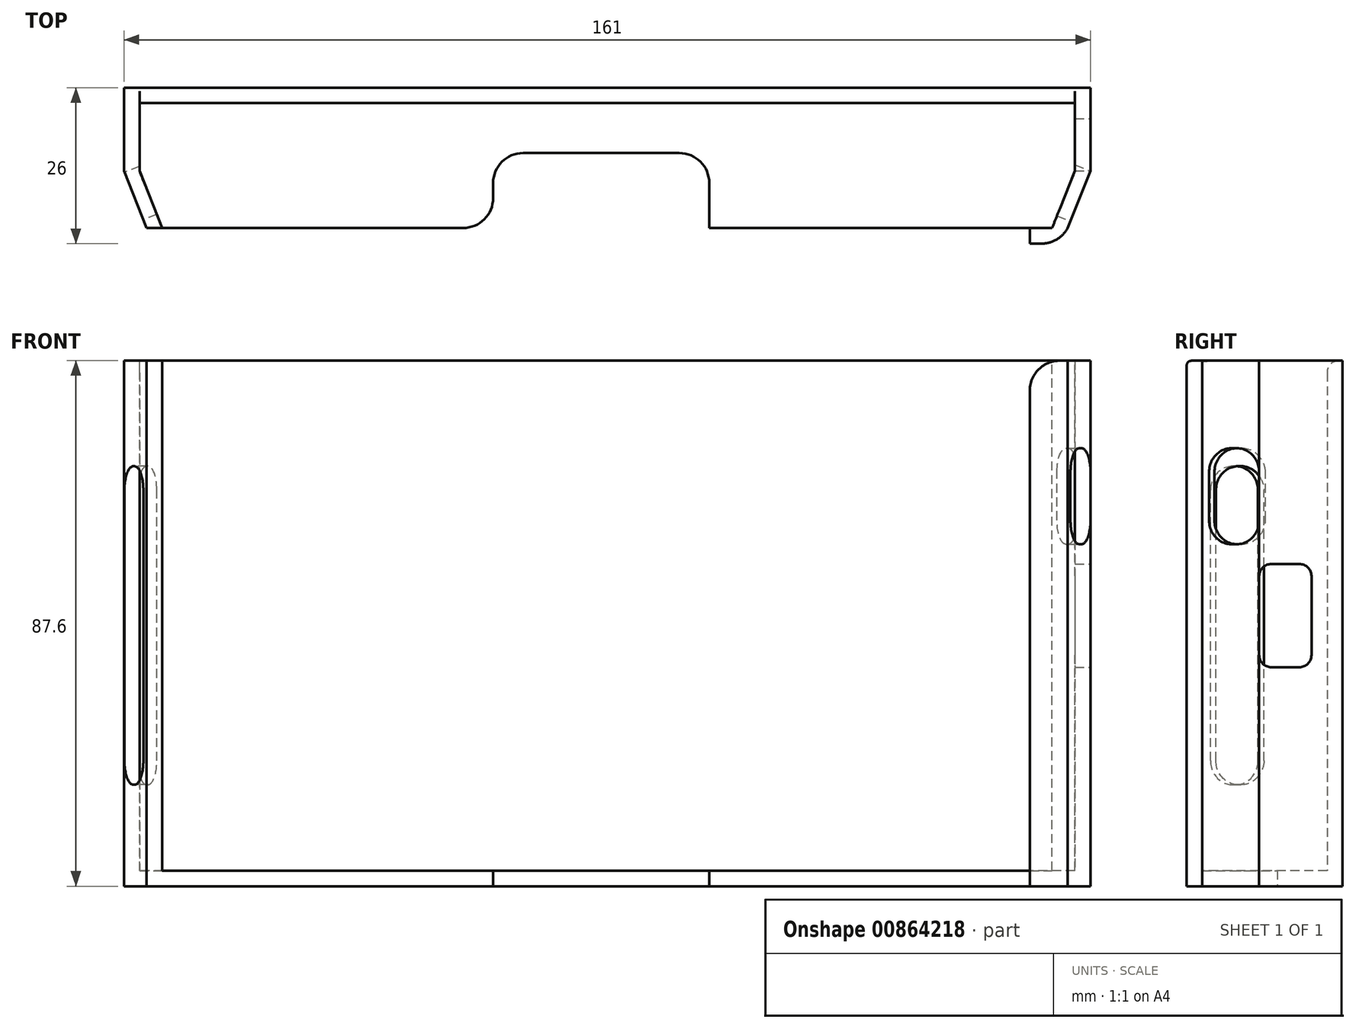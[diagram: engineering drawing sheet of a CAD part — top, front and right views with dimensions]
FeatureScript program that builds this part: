
annotation { "Feature Type Name" : "Feature", "Feature Type Description" : "" }
export const myFeature = defineFeature(function(context is Context, id is Id, definition is map)
    precondition{}
    {
        {
            var Q0;
            Q0=qCreatedBy(makeId("Front.planeOp"),FACE);
            var sketch = newSketch(context, id + "F0", { "sketchPlane" : qUnion([Q0])});
            skLineSegment(sketch, "E0.bottom", {"start": v(77.9, 42.5) * mm, "end": v(-77.9, 42.5) * mm});
            skLineSegment(sketch, "E0.top", {"start": v(77.9, -42.5) * mm, "end": v(-77.9, -42.5) * mm});
            skLineSegment(sketch, "E0.left", {"start": v(77.9, 42.5) * mm, "end": v(77.9, -42.5) * mm});
            skLineSegment(sketch, "E0.right", {"start": v(-77.9, 42.5) * mm, "end": v(-77.9, -42.5) * mm});
            skPoint(sketch, "E0.middle", {"position": v(0, 0) * mm});
            skSolve(sketch);
        }
        {
            var Q0;
            Q0=makeQuery(id+"F0.imprint","IMPRINT",FACE,{"disambiguationData":[TD([[makeQuery(id+"F0.imprint","IMPRINT",EDGE,{"derivedFrom":sQuery(id+"F0.wireOp",EDGE,"E0.bottom")}),1.0]])]});
            extrude(context, id + "F1", {"entities" : qUnion([Q0]), "depth" : 2.6 * mm, "offsetDistance" : 25 * mm});
        }
        {
            var Q0;
            Q0=makeQuery(id+"F1.opExtrude","SWEPT_FACE",FACE,{"disambiguationData":[OSD([sQuery(id+"F0.wireOp",EDGE,"E0.bottom")])]});
            var sketch = newSketch(context, id + "F2", { "sketchPlane" : qUnion([Q0])});
            skLineSegment(sketch, "E1", {"start": v(-77.9, -2.6) * mm, "end": v(-77.9, -13.9) * mm});
            skLineSegment(sketch, "E2", {"start": v(-77.9, -13.9) * mm, "end": v(-80.5, -13.9) * mm});
            skLineSegment(sketch, "E3", {"start": v(-80.5, -13.9) * mm, "end": v(-80.5, 0) * mm});
            skLineSegment(sketch, "E4", {"start": v(-80.5, 0) * mm, "end": v(-77.9, 0) * mm});
            skLineSegment(sketch, "E5", {"start": v(-77.9, -13.9) * mm, "end": v(-77.9, -23.4) * mm, "construction": true});
            skLineSegment(sketch, "E6", {"start": v(-77.9, -23.4) * mm, "end": v(-74.1, -23.4) * mm, "construction": true});
            skLineSegment(sketch, "E7", {"start": v(-77.9, -13.9) * mm, "end": v(-74.1, -23.4) * mm});
            skLineSegment(sketch, "E8", {"start": v(-74.1, -23.4) * mm, "end": v(-76.7, -23.4) * mm});
            skLineSegment(sketch, "E9", {"start": v(-76.7, -23.4) * mm, "end": v(-80.5, -13.9) * mm});
            skLineSegment(sketch, "E10.MirrorCS", {"start": v(77.9, -2.6) * mm, "end": v(77.9, -13.9) * mm});
            skLineSegment(sketch, "E11.MirrorCS", {"start": v(80.5, -13.9) * mm, "end": v(80.5, 0) * mm});
            skLineSegment(sketch, "E12.MirrorCS", {"start": v(76.7, -23.4) * mm, "end": v(80.5, -13.9) * mm});
            skLineSegment(sketch, "E13.MirrorCS", {"start": v(77.9, -13.9) * mm, "end": v(74.1, -23.4) * mm});
            skLineSegment(sketch, "E14.MirrorCS", {"start": v(80.5, 0) * mm, "end": v(77.9, 0) * mm});
            skLineSegment(sketch, "E15", {"start": v(74.1, -23.4) * mm, "end": v(76.7, -23.4) * mm});
            skSolve(sketch);
        }
        {
            var Q0;
            Q0=makeQuery(id+"F2.imprint","IMPRINT",FACE,{"disambiguationData":[TD([[makeQuery(id+"F2.imprint","IMPRINT",EDGE,{"derivedFrom":sQuery(id+"F2.wireOp",EDGE,"E1")}),-1.0]])]});
            var Q1;
            Q1=makeQuery(id+"F2.imprint","IMPRINT",FACE,{"disambiguationData":[TD([[makeQuery(id+"F2.imprint","IMPRINT",EDGE,{"derivedFrom":sQuery(id+"F2.wireOp",EDGE,"E2")}),1.0]])]});
            var Q2;
            Q2=makeQuery(id+"F2.imprint","IMPRINT",FACE,{"disambiguationData":[TD([[makeQuery(id+"F2.imprint","IMPRINT",EDGE,{"derivedFrom":sQuery(id+"F2.wireOp",EDGE,"E10.MirrorCS")}),1.0]])]});
            extrude(context, id + "F3", {"entities" : qUnion([Q0, Q1, Q2]), "operationType" : NewBodyOperationType.ADD, "oppositeDirection" : true, "depth" : 85 * mm, "offsetDistance" : 25 * mm});
        }
        {
            var Q0;
            {var subQ0=sQuery(id+"F0.wireOp",EDGE,"E0.bottom");Q0=makeQuery(id+"F3.boolean.opBoolean","MERGE",FACE,{"derivedFrom":[makeQuery(id+"F1.opExtrude","SWEPT_FACE",FACE,{"disambiguationData":[OSD([sQuery(id+"F0.wireOp",EDGE,"E0.top")])]}),makeQuery(id+"F3.opExtrude","CAP_FACE",FACE,{"disambiguationData":[OSD([subQ0,sQuery(id+"F0.wireOp",EDGE,"E0.right"),sQuery(id+"F2.wireOp",EDGE,"E1"),sQuery(id+"F2.wireOp",EDGE,"E3"),sQuery(id+"F2.wireOp",EDGE,"E4"),sQuery(id+"F2.wireOp",EDGE,"E7"),sQuery(id+"F2.wireOp",EDGE,"E8"),sQuery(id+"F2.wireOp",EDGE,"E9")])],"isStart":false}),makeQuery(id+"F3.opExtrude","CAP_FACE",FACE,{"disambiguationData":[OSD([subQ0,sQuery(id+"F0.wireOp",EDGE,"E0.left"),sQuery(id+"F2.wireOp",EDGE,"E10.MirrorCS"),sQuery(id+"F2.wireOp",EDGE,"E11.MirrorCS"),sQuery(id+"F2.wireOp",EDGE,"E12.MirrorCS"),sQuery(id+"F2.wireOp",EDGE,"E13.MirrorCS"),sQuery(id+"F2.wireOp",EDGE,"E14.MirrorCS"),sQuery(id+"F2.wireOp",EDGE,"E15")])],"isStart":false})]});}
            var sketch = newSketch(context, id + "F4", { "sketchPlane" : qUnion([Q0])});
            skLineSegment(sketch, "E16", {"start": v(-74.1, 23.4) * mm, "end": v(74.1, 23.4) * mm});
            skLineSegment(sketch, "E17", {"start": v(74.1, 23.4) * mm, "end": v(76.7, 23.4) * mm});
            skLineSegment(sketch, "E18", {"start": v(76.7, 23.4) * mm, "end": v(80.5, 13.9) * mm});
            skLineSegment(sketch, "E19", {"start": v(80.5, 13.9) * mm, "end": v(80.5, 0) * mm});
            skLineSegment(sketch, "E20", {"start": v(80.5, 0) * mm, "end": v(-80.5, 0) * mm});
            skLineSegment(sketch, "E21", {"start": v(-80.5, 0) * mm, "end": v(-80.5, 13.9) * mm});
            skLineSegment(sketch, "E22", {"start": v(-80.5, 13.9) * mm, "end": v(-76.7, 23.4) * mm});
            skLineSegment(sketch, "E23", {"start": v(-76.7, 23.4) * mm, "end": v(-74.1, 23.4) * mm});
            skSolve(sketch);
        }
        {
            var Q0;
            Q0=makeQuery(id+"F4.imprint","IMPRINT",FACE,{"disambiguationData":[TD([[makeQuery(id+"F4.imprint","IMPRINT",EDGE,{"derivedFrom":sQuery(id+"F4.wireOp",EDGE,"E16")}),-1.0]])]});
            var Q1;
            Q1=makeQuery(id+"F4.imprint","IMPRINT",FACE,{"disambiguationData":[TD([[makeQuery(id+"F4.imprint","IMPRINT",EDGE,{"derivedFrom":sQuery(id+"F4.wireOp",EDGE,"E17")}),-1.0]])]});
            extrude(context, id + "F5", {"entities" : qUnion([Q0, Q1]), "operationType" : NewBodyOperationType.ADD, "depth" : 2.6 * mm, "offsetDistance" : 25 * mm});
        }
        {
            var Q0;
            Q0=makeQuery(id+"F5.boolean.opBoolean","MERGE",FACE,{"derivedFrom":[makeQuery(id+"F3.opExtrude","SWEPT_FACE",FACE,{"disambiguationData":[OSD([sQuery(id+"F2.wireOp",EDGE,"E11.MirrorCS")])]}),makeQuery(id+"F5.opExtrude","SWEPT_FACE",FACE,{"disambiguationData":[OSD([sQuery(id+"F4.wireOp",EDGE,"E19")])]})]});
            var sketch = newSketch(context, id + "F6", { "sketchPlane" : qUnion([Q0])});
            skLineSegment(sketch, "E24.bottom", {"start": v(-13.9, 8.6) * mm, "end": v(-5.2, 8.6) * mm});
            skLineSegment(sketch, "E24.top", {"start": v(-13.9, -8.6) * mm, "end": v(-5.2, -8.6) * mm});
            skLineSegment(sketch, "E24.left", {"start": v(-13.9, 8.6) * mm, "end": v(-13.9, -8.6) * mm});
            skLineSegment(sketch, "E24.right", {"start": v(-5.2, 8.6) * mm, "end": v(-5.2, -8.6) * mm});
            skSolve(sketch);
        }
        {
            var Q0;
            Q0=makeQuery(id+"F6.imprint","IMPRINT",FACE,{"disambiguationData":[TD([[makeQuery(id+"F6.imprint","IMPRINT",EDGE,{"derivedFrom":sQuery(id+"F6.wireOp",EDGE,"E24.bottom")}),-1.0]])]});
            extrude(context, id + "F7", {"entities" : qUnion([Q0]), "operationType" : NewBodyOperationType.REMOVE, "oppositeDirection" : true, "depth" : 25 * mm, "offsetDistance" : 25 * mm});
        }
        {
            var Q0;
            Q0=makeQuery(id+"F5.boolean.opBoolean","MERGE",FACE,{"derivedFrom":[makeQuery(id+"F3.opExtrude","SWEPT_FACE",FACE,{"disambiguationData":[OSD([sQuery(id+"F2.wireOp",EDGE,"E12.MirrorCS")])]}),makeQuery(id+"F5.opExtrude","SWEPT_FACE",FACE,{"disambiguationData":[OSD([sQuery(id+"F4.wireOp",EDGE,"E18")])]})]});
            var sketch = newSketch(context, id + "F8", { "sketchPlane" : qUnion([Q0])});
            skLineSegment(sketch, "E25.bottom", {"start": v(17, 27.9) * mm, "end": v(8, 27.9) * mm});
            skLineSegment(sketch, "E25.top", {"start": v(17, 11.9) * mm, "end": v(8, 11.9) * mm});
            skLineSegment(sketch, "E25.left", {"start": v(17, 27.9) * mm, "end": v(17, 11.9) * mm});
            skLineSegment(sketch, "E25.right", {"start": v(8, 27.9) * mm, "end": v(8, 11.9) * mm});
            skSolve(sketch);
        }
        {
            var Q0;
            Q0=makeQuery(id+"F8.imprint","IMPRINT",FACE,{"disambiguationData":[TD([[makeQuery(id+"F8.imprint","IMPRINT",EDGE,{"derivedFrom":sQuery(id+"F8.wireOp",EDGE,"E25.bottom")}),1.0]])]});
            extrude(context, id + "F9", {"entities" : qUnion([Q0]), "operationType" : NewBodyOperationType.REMOVE, "oppositeDirection" : true, "depth" : 25 * mm, "offsetDistance" : 25 * mm});
        }
        {
            var Q0;
            Q0=makeQuery(id+"F5.boolean.opBoolean","MERGE",FACE,{"derivedFrom":[makeQuery(id+"F3.opExtrude","SWEPT_FACE",FACE,{"disambiguationData":[OSD([sQuery(id+"F2.wireOp",EDGE,"E9")])]}),makeQuery(id+"F5.opExtrude","SWEPT_FACE",FACE,{"disambiguationData":[OSD([sQuery(id+"F4.wireOp",EDGE,"E22")])]})]});
            var sketch = newSketch(context, id + "F10", { "sketchPlane" : qUnion([Q0])});
            skLineSegment(sketch, "E26.bottom", {"start": v(-8.26, -28.2) * mm, "end": v(-16.76, -28.2) * mm});
            skLineSegment(sketch, "E26.top", {"start": v(-8.26, 24.9) * mm, "end": v(-16.76, 24.9) * mm});
            skLineSegment(sketch, "E26.left", {"start": v(-8.26, -28.2) * mm, "end": v(-8.26, 24.9) * mm});
            skLineSegment(sketch, "E26.right", {"start": v(-16.76, -28.2) * mm, "end": v(-16.76, 24.9) * mm});
            skSolve(sketch);
        }
        {
            var Q0;
            Q0=makeQuery(id+"F10.imprint","IMPRINT",FACE,{"disambiguationData":[TD([[makeQuery(id+"F10.imprint","IMPRINT",EDGE,{"derivedFrom":sQuery(id+"F10.wireOp",EDGE,"E26.bottom")}),-1.0]])]});
            extrude(context, id + "F11", {"entities" : qUnion([Q0]), "operationType" : NewBodyOperationType.REMOVE, "oppositeDirection" : true, "depth" : 25 * mm, "offsetDistance" : 25 * mm});
        }
        {
            var Q0;
            Q0=makeQuery(id+"FsZxfdEWeTOnJij_3.opBoolean","MERGE",FACE,{"derivedFrom":[makeQuery(id+"FqDJVQkYOp9GbU9_1.opExtrude","SWEPT_FACE",FACE,{"disambiguationData":[OSD([sQuery(id+"FvzB3UYrsBdap8L_1.wireOp",EDGE,"Uml6c2Dv-acHc-Gifl-ZtFl-aoH73OwEvOf2.top")])]}),makeQuery(id+"FhGYIp8tMEhZQ6G_2.boolean.opBoolean","MERGE",FACE,{"derivedFrom":[makeQuery(id+"F5.opExtrude","CAP_FACE",FACE,{"disambiguationData":[OSD([sQuery(id+"F4.wireOp",EDGE,"E16"),sQuery(id+"F4.wireOp",EDGE,"E17"),sQuery(id+"F4.wireOp",EDGE,"E18"),sQuery(id+"F4.wireOp",EDGE,"E19"),sQuery(id+"F4.wireOp",EDGE,"E20"),sQuery(id+"F4.wireOp",EDGE,"E21"),sQuery(id+"F4.wireOp",EDGE,"E22"),sQuery(id+"F4.wireOp",EDGE,"E23")])],"isStart":false}),makeQuery(id+"FhGYIp8tMEhZQ6G_2.opExtrude","SWEPT_FACE",FACE,{"disambiguationData":[OSD([sQuery(id+"FduUudokjhFXSVZ_2.wireOp",EDGE,"elEno3Yk-yd7y-Hb1z-syM6-87jU7vVd34ST.top")])]})]}),makeQuery(id+"Fz9UfncQxzrdPbm_2.opExtrude","SWEPT_FACE",FACE,{"disambiguationData":[OSD([sQuery(id+"Fw4ObimbiuuVDjj_2.wireOp",EDGE,"KRR7Us3h-wgd5-YgCl-ZbNL-mRqCgfLZCEfi.top")])]})]});
            var sketch = newSketch(context, id + "F12", { "sketchPlane" : qUnion([Q0])});
            skLineSegment(sketch, "E27.bottom", {"start": v(-19, 23.4) * mm, "end": v(17, 23.4) * mm});
            skLineSegment(sketch, "E27.top", {"start": v(-19, 10.9) * mm, "end": v(17, 10.9) * mm});
            skLineSegment(sketch, "E27.left", {"start": v(-19, 23.4) * mm, "end": v(-19, 10.9) * mm});
            skLineSegment(sketch, "E27.right", {"start": v(17, 23.4) * mm, "end": v(17, 10.9) * mm});
            skSolve(sketch);
        }
        {
            var Q0;
            Q0=makeQuery(id+"F12.imprint","IMPRINT",FACE,{"disambiguationData":[TD([[makeQuery(id+"F12.imprint","IMPRINT",EDGE,{"derivedFrom":sQuery(id+"F12.wireOp",EDGE,"E27.bottom")}),-1.0]])]});
            extrude(context, id + "F13", {"entities" : qUnion([Q0]), "operationType" : NewBodyOperationType.REMOVE, "oppositeDirection" : true, "depth" : 25 * mm, "offsetDistance" : 25 * mm});
        }
        {
            var Q0;
            Q0=makeQuery(id+"F11.boolean.opBoolean","COPY",EDGE,{"derivedFrom":makeQuery(id+"F11.opExtrude","SWEPT_EDGE",EDGE,{"disambiguationData":[OSD([sQuery(id+"F10.wireOp",EDGE,"E26.bottom"),sQuery(id+"F10.wireOp",EDGE,"E26.right")])]})});
            var Q1;
            Q1=makeQuery(id+"F11.boolean.opBoolean","COPY",EDGE,{"derivedFrom":makeQuery(id+"F11.opExtrude","SWEPT_EDGE",EDGE,{"disambiguationData":[OSD([sQuery(id+"F10.wireOp",EDGE,"E26.bottom"),sQuery(id+"F10.wireOp",EDGE,"E26.left")])]})});
            var Q2;
            Q2=makeQuery(id+"F11.boolean.opBoolean","COPY",EDGE,{"derivedFrom":makeQuery(id+"F11.opExtrude","SWEPT_EDGE",EDGE,{"disambiguationData":[OSD([sQuery(id+"F10.wireOp",EDGE,"E26.top"),sQuery(id+"F10.wireOp",EDGE,"E26.left")])]})});
            var Q3;
            Q3=makeQuery(id+"F11.boolean.opBoolean","COPY",EDGE,{"derivedFrom":makeQuery(id+"F11.opExtrude","SWEPT_EDGE",EDGE,{"disambiguationData":[OSD([sQuery(id+"F10.wireOp",EDGE,"E26.top"),sQuery(id+"F10.wireOp",EDGE,"E26.right")])]})});
            fillet(context, id + "F14", {"entities" : qUnion([Q0, Q1, Q2, Q3]), "radius" : 4 * mm, "tangentPropagation" : true, "allowEdgeOverflow" : false});
        }
        {
            var Q0;
            Q0=makeQuery(id+"F9.boolean.opBoolean","COPY",EDGE,{"derivedFrom":makeQuery(id+"F9.opExtrude","SWEPT_EDGE",EDGE,{"disambiguationData":[OSD([sQuery(id+"F8.wireOp",EDGE,"E25.top"),sQuery(id+"F8.wireOp",EDGE,"E25.right")])]})});
            var Q1;
            Q1=makeQuery(id+"F9.boolean.opBoolean","COPY",EDGE,{"derivedFrom":makeQuery(id+"F9.opExtrude","SWEPT_EDGE",EDGE,{"disambiguationData":[OSD([sQuery(id+"F2.wireOp",EDGE,"E11.MirrorCS"),sQuery(id+"F2.wireOp",EDGE,"E12.MirrorCS"),sQuery(id+"F4.wireOp",EDGE,"E18"),sQuery(id+"F4.wireOp",EDGE,"E19"),sQuery(id+"F8.wireOp",EDGE,"E25.top"),sQuery(id+"F8.wireOp",EDGE,"E25.left")])]})});
            var Q2;
            Q2=makeQuery(id+"F9.boolean.opBoolean","COPY",EDGE,{"derivedFrom":makeQuery(id+"F9.opExtrude","SWEPT_EDGE",EDGE,{"disambiguationData":[OSD([sQuery(id+"F8.wireOp",EDGE,"E25.bottom"),sQuery(id+"F8.wireOp",EDGE,"E25.right")])]})});
            var Q3;
            Q3=makeQuery(id+"F9.boolean.opBoolean","COPY",EDGE,{"derivedFrom":makeQuery(id+"F9.opExtrude","SWEPT_EDGE",EDGE,{"disambiguationData":[OSD([sQuery(id+"F2.wireOp",EDGE,"E11.MirrorCS"),sQuery(id+"F2.wireOp",EDGE,"E12.MirrorCS"),sQuery(id+"F4.wireOp",EDGE,"E18"),sQuery(id+"F4.wireOp",EDGE,"E19"),sQuery(id+"F8.wireOp",EDGE,"E25.bottom"),sQuery(id+"F8.wireOp",EDGE,"E25.left")])]})});
            fillet(context, id + "F15", {"entities" : qUnion([Q0, Q1, Q2, Q3]), "radius" : 4 * mm, "tangentPropagation" : true, "allowEdgeOverflow" : false});
        }
        {
            var Q0;
            Q0=makeQuery(id+"F7.boolean.opBoolean","COPY",EDGE,{"derivedFrom":makeQuery(id+"F7.opExtrude","SWEPT_EDGE",EDGE,{"disambiguationData":[OSD([sQuery(id+"F2.wireOp",EDGE,"E11.MirrorCS"),sQuery(id+"F2.wireOp",EDGE,"E12.MirrorCS"),sQuery(id+"F4.wireOp",EDGE,"E18"),sQuery(id+"F4.wireOp",EDGE,"E19"),sQuery(id+"F6.wireOp",EDGE,"E24.bottom"),sQuery(id+"F6.wireOp",EDGE,"E24.left")])]})});
            var Q1;
            Q1=makeQuery(id+"F7.boolean.opBoolean","COPY",EDGE,{"derivedFrom":makeQuery(id+"F7.opExtrude","SWEPT_EDGE",EDGE,{"disambiguationData":[OSD([sQuery(id+"F6.wireOp",EDGE,"E24.bottom"),sQuery(id+"F6.wireOp",EDGE,"E24.right")])]})});
            var Q2;
            Q2=makeQuery(id+"F7.boolean.opBoolean","COPY",EDGE,{"derivedFrom":makeQuery(id+"F7.opExtrude","SWEPT_EDGE",EDGE,{"disambiguationData":[OSD([sQuery(id+"F6.wireOp",EDGE,"E24.top"),sQuery(id+"F6.wireOp",EDGE,"E24.right")])]})});
            var Q3;
            Q3=makeQuery(id+"F7.boolean.opBoolean","COPY",EDGE,{"derivedFrom":makeQuery(id+"F7.opExtrude","SWEPT_EDGE",EDGE,{"disambiguationData":[OSD([sQuery(id+"F2.wireOp",EDGE,"E11.MirrorCS"),sQuery(id+"F2.wireOp",EDGE,"E12.MirrorCS"),sQuery(id+"F4.wireOp",EDGE,"E18"),sQuery(id+"F4.wireOp",EDGE,"E19"),sQuery(id+"F6.wireOp",EDGE,"E24.top"),sQuery(id+"F6.wireOp",EDGE,"E24.left")])]})});
            fillet(context, id + "F16", {"entities" : qUnion([Q0, Q1, Q2, Q3]), "radius" : 2 * mm, "tangentPropagation" : true, "allowEdgeOverflow" : false});
        }
        {
            var Q0;
            Q0=makeQuery(id+"F13.boolean.opBoolean","COPY",EDGE,{"derivedFrom":makeQuery(id+"F13.opExtrude","SWEPT_EDGE",EDGE,{"disambiguationData":[OSD([sQuery(id+"F12.wireOp",EDGE,"E27.top"),sQuery(id+"F12.wireOp",EDGE,"E27.right")])]})});
            var Q1;
            Q1=makeQuery(id+"F13.boolean.opBoolean","COPY",EDGE,{"derivedFrom":makeQuery(id+"F13.opExtrude","SWEPT_EDGE",EDGE,{"disambiguationData":[OSD([sQuery(id+"F12.wireOp",EDGE,"E27.top"),sQuery(id+"F12.wireOp",EDGE,"E27.left")])]})});
            var Q2;
            Q2=makeQuery(id+"F13.boolean.opBoolean","COPY",EDGE,{"derivedFrom":makeQuery(id+"F13.opExtrude","SWEPT_EDGE",EDGE,{"disambiguationData":[OSD([sQuery(id+"F4.wireOp",EDGE,"E16"),sQuery(id+"F4.wireOp",EDGE,"E17"),sQuery(id+"F4.wireOp",EDGE,"E23"),sQuery(id+"F12.wireOp",EDGE,"E27.bottom"),sQuery(id+"F12.wireOp",EDGE,"E27.right")])]})});
            var Q3;
            Q3=makeQuery(id+"F13.boolean.opBoolean","COPY",EDGE,{"derivedFrom":makeQuery(id+"F13.opExtrude","SWEPT_EDGE",EDGE,{"disambiguationData":[OSD([sQuery(id+"F4.wireOp",EDGE,"E16"),sQuery(id+"F4.wireOp",EDGE,"E17"),sQuery(id+"F4.wireOp",EDGE,"E23"),sQuery(id+"F12.wireOp",EDGE,"E27.bottom"),sQuery(id+"F12.wireOp",EDGE,"E27.left")])]})});
            fillet(context, id + "F17", {"entities" : qUnion([Q0, Q1, Q2, Q3]), "radius" : 5 * mm, "tangentPropagation" : true, "allowEdgeOverflow" : false});
        }
        {
            var Q0;
            Q0=makeQuery(id+"F1.opExtrude","CAP_EDGE",EDGE,{"disambiguationData":[OSD([sQuery(id+"F0.wireOp",EDGE,"E0.bottom")])],"isStart":false});
            var Q1;
            Q1=makeQuery(id+"Fz9UfncQxzrdPbm_2.opExtrude","CAP_EDGE",EDGE,{"disambiguationData":[OSD([sQuery(id+"Fw4ObimbiuuVDjj_2.wireOp",EDGE,"KRR7Us3h-wgd5-YgCl-ZbNL-mRqCgfLZCEfi.bottom")])],"isStart":false});
            fillet(context, id + "F18", {"entities" : qUnion([Q0, Q1]), "radius" : 2 * mm, "tangentPropagation" : true, "allowEdgeOverflow" : false});
        }
        {
            var Q0;
            Q0=makeQuery(id+"F5.opExtrude","CAP_FACE",FACE,{"disambiguationData":[OSD([sQuery(id+"F4.wireOp",EDGE,"E16"),sQuery(id+"F4.wireOp",EDGE,"E17"),sQuery(id+"F4.wireOp",EDGE,"E18"),sQuery(id+"F4.wireOp",EDGE,"E19"),sQuery(id+"F4.wireOp",EDGE,"E20"),sQuery(id+"F4.wireOp",EDGE,"E21"),sQuery(id+"F4.wireOp",EDGE,"E22"),sQuery(id+"F4.wireOp",EDGE,"E23")])],"isStart":false});
            var sketch = newSketch(context, id + "F19", { "sketchPlane" : qUnion([Q0])});
            skLineSegment(sketch, "E28", {"start": v(76.7, 23.4) * mm, "end": v(76.7, 26) * mm});
            skLineSegment(sketch, "E29", {"start": v(76.7, 26) * mm, "end": v(70.4, 26) * mm});
            skLineSegment(sketch, "E30", {"start": v(70.4, 26) * mm, "end": v(70.4, 24.37) * mm});
            skLineSegment(sketch, "E31", {"start": v(70.4, 24.37) * mm, "end": v(70.4, 23.4) * mm});
            skSolve(sketch);
        }
        {
            var Q0;
            {var subQ1=sQuery(id+"F19.wireOp",EDGE,"E28");Q0=makeQuery(id+"F19.imprint","IMPRINT",FACE,{"disambiguationData":[TD([[makeQuery(id+"F19.imprint","IMPRINT",EDGE,{"derivedFrom":subQ1}),1.0]])]});}
            extrude(context, id + "F20", {"entities" : qUnion([Q0]), "operationType" : NewBodyOperationType.ADD, "oppositeDirection" : true, "depth" : 87.6 * mm, "offsetDistance" : 25 * mm});
        }
        {
            var Q0;
            Q0=makeQuery(id+"F20.opExtrude","CAP_EDGE",EDGE,{"disambiguationData":[OSD([sQuery(id+"F19.wireOp",EDGE,"E30"),sQuery(id+"F19.wireOp",EDGE,"E31")])],"isStart":false});
            fillet(context, id + "F21", {"entities" : qUnion([Q0]), "radius" : 5 * mm, "tangentPropagation" : true, "allowEdgeOverflow" : false});
        }
        {
            var Q0;
            Q0=makeQuery(id+"F20.opExtrude","SWEPT_EDGE",EDGE,{"disambiguationData":[OSD([sQuery(id+"F19.wireOp",EDGE,"E28"),sQuery(id+"F19.wireOp",EDGE,"E29")])]});
            fillet(context, id + "F22", {"entities" : qUnion([Q0]), "radius" : 5 * mm, "tangentPropagation" : true, "allowEdgeOverflow" : false});
        }
    });
